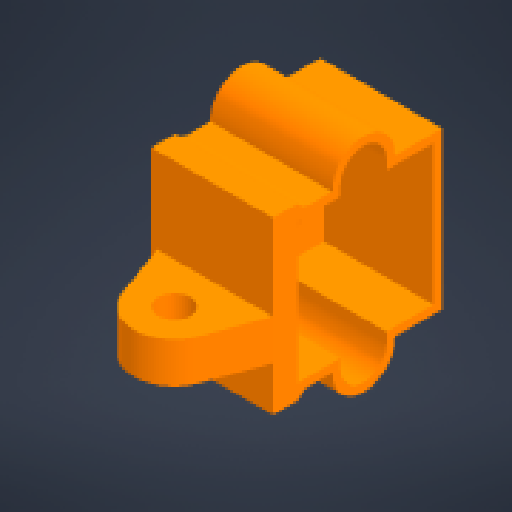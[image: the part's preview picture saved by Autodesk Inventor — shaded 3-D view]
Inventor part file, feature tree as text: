
AUTODESK INVENTOR PART (.ipt)
format: ipt  version: 2024 (Build 280153000, 153)  size: 241,152 bytes
history: native  units: mm
features: reference x6, other x5, extrude x4, sketch x4, fillet x1, projected_geometry x1
ambient origin geometry x8: Origin, YZ Plane, XZ Plane, XY Plane, X Axis, Y Axis, Z Axis, Center Point
bodies: Body1 (feature_tree)
feature tree (21):
  other  "Твердое тело1"
  extrude  "Выдавливание1"  Depth=14.28148mm
  extrude  "Выдавливание2"  Depth=14.28148mm
  extrude  "Выдавливание3"  Depth=6.710101mm
  extrude  "Выдавливание4"  Depth=6.710101mm
  fillet  "Сопряжение1"  Radius=12.217305mm
  sketch  "Эскиз1"
  reference  "Ссылка1"
  reference  "Ссылка2"
  sketch  "Эскиз2"
  sketch  "Эскиз3"
  reference  "Ссылка3"
  sketch  "Эскиз4"
  reference  "Ссылка4"
  reference  "Ссылка5"
  reference  "Ссылка6"
  projected_geometry  "Спроецированная петля1"
  parser-record x1  (decoder bookkeeping rows leaked as tree rows — omitted from the tree; the rows remain in map.json)
  other  "cum_holder_asembly.iam"
  other  "cum_holder_down:1"
  other  "cum:1"
note: 1 file-system path scrubbed to <path> (originals preserved in map.json)
